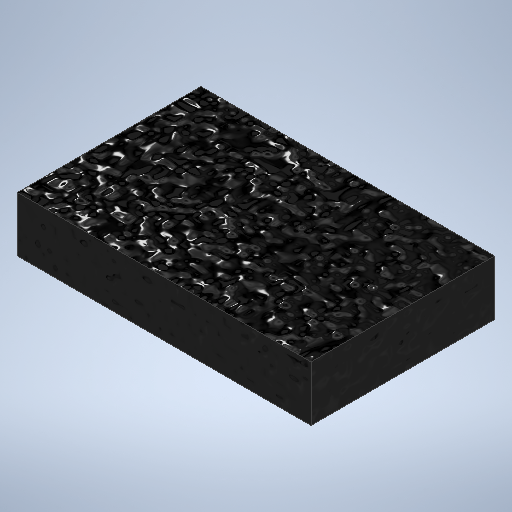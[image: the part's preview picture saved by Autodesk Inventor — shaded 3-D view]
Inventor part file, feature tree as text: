
AUTODESK INVENTOR PART (.ipt)
format: ipt  version: 2025.1 (Build 291241000, 241)  size: 290,816 bytes
history: native  units: in
note: dims shown in document units (in); Inventor stores cm internally (conversion verified against a paired STEP export)
features: extrude x1, sketch x1, other x1
ambient origin geometry x8: Origin, YZ Plane, XZ Plane, XY Plane, X Axis, Y Axis, Z Axis, Center Point
bodies: Solid1 (feature_tree)
feature tree (3):
  extrude  "Extrusion1"  Depth=3.937in
  sketch  "Sketch1"  dims[d0=6.2992in d1=3.937in d2=1.1811in d3=0.0in]
  other  "Finish1"
